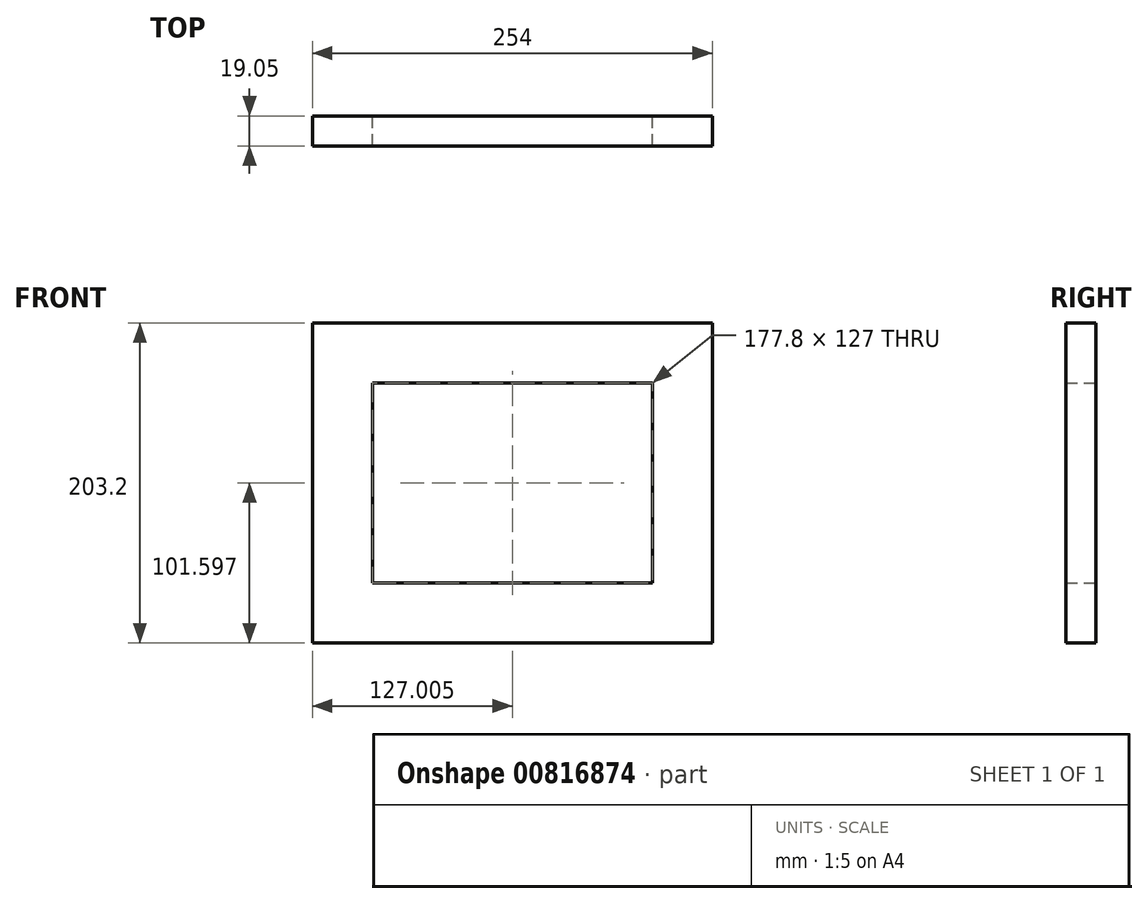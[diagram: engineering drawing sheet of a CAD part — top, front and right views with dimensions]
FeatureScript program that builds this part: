
annotation { "Feature Type Name" : "Feature", "Feature Type Description" : "" }
export const myFeature = defineFeature(function(context is Context, id is Id, definition is map)
    precondition{}
    {
        {
            var Q0;
            Q0=qCreatedBy(makeId("Front.planeOp"),FACE);
            var sketch = newSketch(context, id + "F0", { "sketchPlane" : qUnion([Q0])});
            skLineSegment(sketch, "E0.bottom", {"start": v(-135.15, 112.9) * mm, "end": v(118.85, 112.9) * mm});
            skLineSegment(sketch, "E0.top", {"start": v(-135.15, -90.3) * mm, "end": v(118.85, -90.3) * mm});
            skLineSegment(sketch, "E0.left", {"start": v(-135.15, 112.9) * mm, "end": v(-135.15, -90.3) * mm});
            skLineSegment(sketch, "E0.right", {"start": v(118.85, 112.9) * mm, "end": v(118.85, -90.3) * mm});
            skLineSegment(sketch, "E1.0", {"start": v(-97.05, 74.8) * mm, "end": v(80.75, 74.8) * mm});
            skLineSegment(sketch, "E1.1", {"start": v(-97.05, 74.8) * mm, "end": v(-97.05, -52.2) * mm});
            skLineSegment(sketch, "E1.2", {"start": v(-97.05, -52.2) * mm, "end": v(80.75, -52.2) * mm});
            skLineSegment(sketch, "E1.3", {"start": v(80.75, 74.8) * mm, "end": v(80.75, -52.2) * mm});
            skSolve(sketch);
        }
        {
            var Q0;
            Q0=makeQuery(id+"F0.imprint","IMPRINT",FACE,{"disambiguationData":[TD([[makeQuery(id+"F0.imprint","IMPRINT",EDGE,{"derivedFrom":sQuery(id+"F0.wireOp",EDGE,"E0.bottom")}),-1.0]])]});
            extrude(context, id + "F1", {"entities" : qUnion([Q0]), "depth" : 19.05 * mm, "offsetDistance" : 25.4 * mm});
        }
    });
